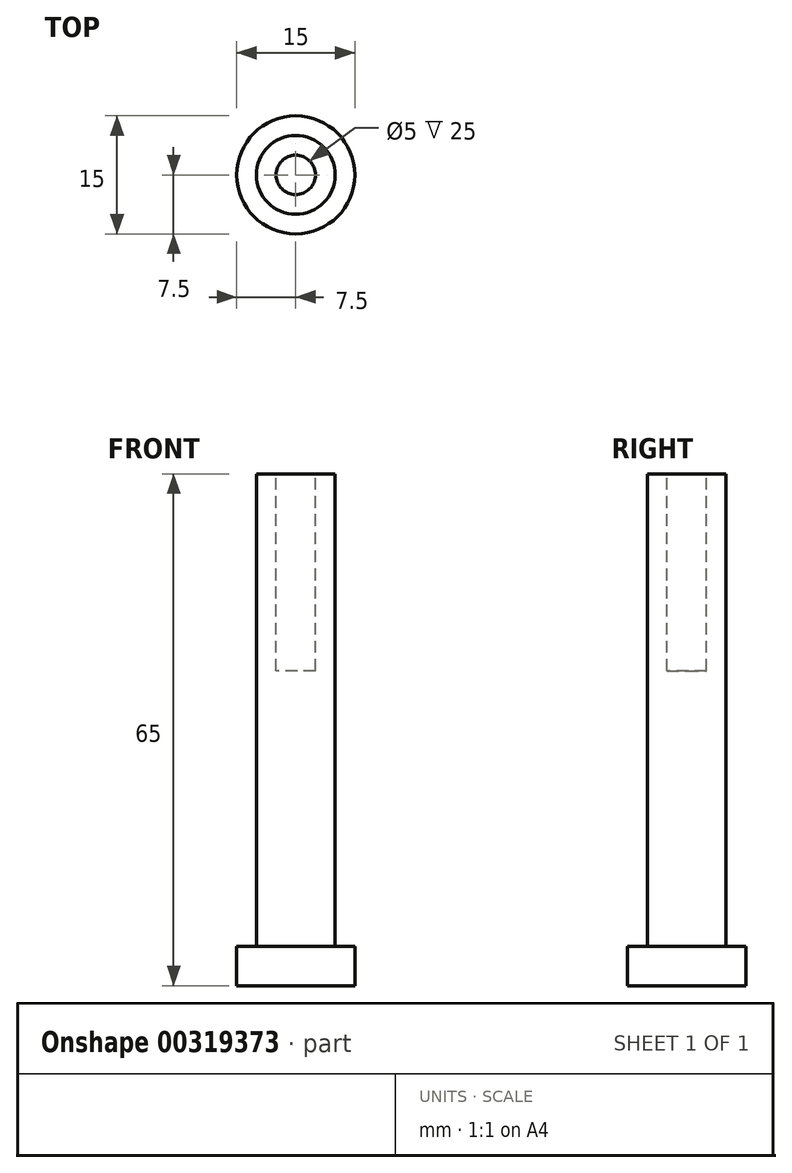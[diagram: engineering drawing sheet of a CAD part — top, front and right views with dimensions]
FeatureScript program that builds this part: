
annotation { "Feature Type Name" : "Feature", "Feature Type Description" : "" }
export const myFeature = defineFeature(function(context is Context, id is Id, definition is map)
    precondition{}
    {
        {
            var Q0;
            Q0=qCreatedBy(makeId("Top.planeOp"),FACE);
            var sketch = newSketch(context, id + "F0", { "sketchPlane" : qUnion([Q0])});
            skCircle(sketch, "E0", {"center": v(0, 0) * mm, "radius": 5 * mm});
            skSolve(sketch);
        }
        {
            var Q0;
            Q0=qSketchRegion(id+"F0",true);
            extrude(context, id + "F1", {"entities" : qUnion([Q0]), "depth" : 60 * mm});
        }
        {
            var Q0;
            Q0=makeQuery(id+"F1.opExtrude","CAP_FACE",FACE,{"disambiguationData":[OSD([sQuery(id+"F0.wireOp",EDGE,"E0")])],"isStart":true});
            var sketch = newSketch(context, id + "F2", { "sketchPlane" : qUnion([Q0])});
            skCircle(sketch, "E1", {"center": v(0, 0) * mm, "radius": 7.5 * mm});
            skSolve(sketch);
        }
        {
            var Q0;
            Q0=makeQuery(id+"F2.imprint","IMPRINT",FACE,{"disambiguationData":[TD([[makeQuery(id+"F2.imprint","IMPRINT",EDGE,{"derivedFrom":sQuery(id+"F2.wireOp",EDGE,"E1")}),1.0]])]});
            var Q1;
            Q1=makeQuery(id+"F2.imprint","IMPRINT",FACE,{"disambiguationData":[TD([[makeQuery(id+"F2.imprint","IMPRINT",EDGE,{"derivedFrom":makeQuery(id+"F1.opExtrude","CAP_EDGE",EDGE,{"disambiguationData":[OSD([sQuery(id+"F0.wireOp",EDGE,"E0")])],"isStart":true})}),-1.0]])]});
            extrude(context, id + "F3", {"entities" : qUnion([Q0, Q1]), "operationType" : NewBodyOperationType.ADD, "depth" : 5 * mm});
        }
        {
            var Q0;
            Q0=makeQuery(id+"F1.opExtrude","CAP_FACE",FACE,{"disambiguationData":[OSD([sQuery(id+"F0.wireOp",EDGE,"E0")])],"isStart":false});
            var sketch = newSketch(context, id + "F4", { "sketchPlane" : qUnion([Q0])});
            skCircle(sketch, "E2", {"center": v(0, 0) * mm, "radius": 2.5 * mm});
            skSolve(sketch);
        }
        {
            var Q0;
            Q0=qSketchRegion(id+"F4",true);
            extrude(context, id + "F5", {"entities" : qUnion([Q0]), "operationType" : NewBodyOperationType.REMOVE, "oppositeDirection" : true, "depth" : 25 * mm});
        }
    });
